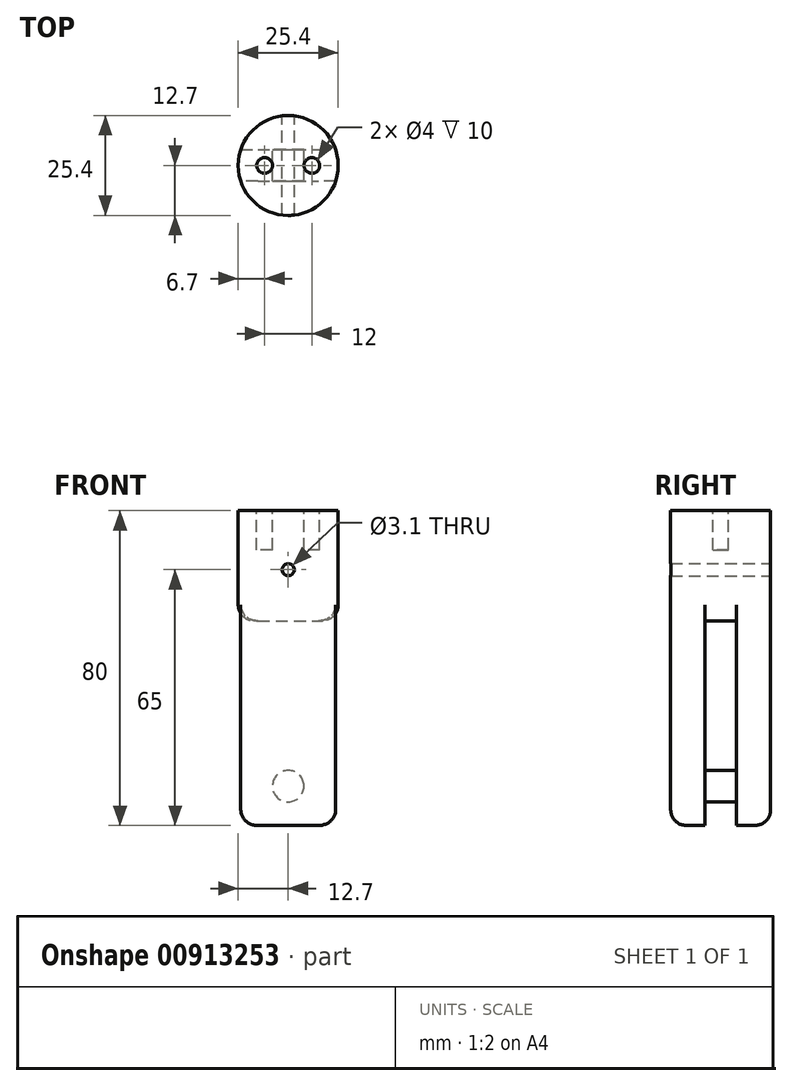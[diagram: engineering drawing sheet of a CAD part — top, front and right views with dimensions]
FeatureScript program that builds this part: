
annotation { "Feature Type Name" : "Feature", "Feature Type Description" : "" }
export const myFeature = defineFeature(function(context is Context, id is Id, definition is map)
    precondition{}
    {
        {
            var Q0;
            Q0=qCreatedBy(makeId("Front.planeOp"),FACE);
            var sketch = newSketch(context, id + "F0", { "sketchPlane" : qUnion([Q0])});
            skCircle(sketch, "E0", {"center": v(0, 0) * mm, "radius": 4 * mm, "construction": true});
            skLineSegment(sketch, "E1.bottom", {"start": v(0, 70) * mm, "end": v(-12.7, 70) * mm});
            skLineSegment(sketch, "E1.top", {"start": v(0, -10) * mm, "end": v(-12.7, -10) * mm});
            skLineSegment(sketch, "E1.left", {"start": v(0, 70) * mm, "end": v(0, -10) * mm});
            skLineSegment(sketch, "E1.right", {"start": v(-12.7, 70) * mm, "end": v(-12.7, -10) * mm});
            skSolve(sketch);
        }
        {
            var Q0;
            Q0=makeQuery(id+"F0.imprint","IMPRINT",FACE,{"disambiguationData":[TD([[makeQuery(id+"F0.imprint","IMPRINT",EDGE,{"derivedFrom":sQuery(id+"F0.wireOp",EDGE,"E1.bottom")}),1.0]])]});
            var Q1;
            Q1=sQuery(id+"F0.wireOp",EDGE,"E1.left");
            revolve(context, id + "F1", {"surfaceOperationType" : NewSurfaceOperationType.NEW, "entities" : qUnion([Q0]), "axis" : qUnion([Q1]), "revolveType" : RevolveType.FULL});
        }
        {
            var Q0;
            Q0=qCreatedBy(makeId("Right.planeOp"),FACE);
            var sketch = newSketch(context, id + "F2", { "sketchPlane" : qUnion([Q0])});
            skPoint(sketch, "E2.0", {"position": v(0, -10) * mm});
            skLineSegment(sketch, "E3.bottom", {"start": v(-4, 42) * mm, "end": v(4, 42) * mm});
            skLineSegment(sketch, "E3.top", {"start": v(-4, -10) * mm, "end": v(4, -10) * mm});
            skLineSegment(sketch, "E3.left", {"start": v(-4, 42) * mm, "end": v(-4, -10) * mm});
            skLineSegment(sketch, "E3.right", {"start": v(4, 42) * mm, "end": v(4, -10) * mm});
            skSolve(sketch);
        }
        {
            var Q0;
            Q0=qSketchRegion(id+"F2",true);
            extrude(context, id + "F3", {"entities" : qUnion([Q0]), "operationType" : NewBodyOperationType.REMOVE, "endBound" : BoundingType.THROUGH_ALL, "oppositeDirection" : true, "depth" : 25 * mm, "offsetDistance" : 25 * mm, "hasSecondDirection" : true, "secondDirectionBound" : SecondDirectionBoundingType.THROUGH_ALL, "secondDirectionOppositeDirection" : false, "secondDirectionDepth" : 25 * mm});
        }
        {
            var Q0;
            Q0=qCreatedBy(makeId("Front.planeOp"),FACE);
            var sketch = newSketch(context, id + "F4", { "sketchPlane" : qUnion([Q0])});
            skCircle(sketch, "E4.0", {"center": v(0, 0) * mm, "radius": 4 * mm});
            skSolve(sketch);
        }
        {
            var Q0;
            Q0=qSketchRegion(id+"F4",true);
            extrude(context, id + "F5", {"entities" : qUnion([Q0]), "operationType" : NewBodyOperationType.ADD, "endBound" : BoundingType.SYMMETRIC, "depth" : 10 * mm, "offsetDistance" : 25 * mm});
        }
        {
            var Q0;
            Q0=makeQuery(id+"F1.opRevolve","SWEPT_FACE",FACE,{"disambiguationData":[OSD([sQuery(id+"F0.wireOp",EDGE,"E1.bottom")])]});
            var sketch = newSketch(context, id + "F6", { "sketchPlane" : qUnion([Q0])});
            skCircle(sketch, "E5", {"center": v(-6, 0) * mm, "radius": 2 * mm});
            skLineSegment(sketch, "E6", {"start": v(0, 0) * mm, "end": v(0, 3.84) * mm});
            skCircle(sketch, "E7.MirrorC", {"center": v(6, 0) * mm, "radius": 2 * mm});
            skSolve(sketch);
        }
        {
            var Q0;
            Q0=qSketchRegion(id+"F6",true);
            extrude(context, id + "F7", {"entities" : qUnion([Q0]), "operationType" : NewBodyOperationType.REMOVE, "oppositeDirection" : true, "depth" : 10 * mm, "offsetDistance" : 25 * mm});
        }
        {
            var Q0;
            Q0=makeQuery(id+"F3.boolean.opBoolean","INTERSECT",EDGE,{"disambiguationData":[OD(0.0)],"derivedFrom":[makeQuery(id+"F1.opRevolve","SWEPT_FACE",FACE,{"disambiguationData":[OSD([sQuery(id+"F0.wireOp",EDGE,"E1.right")])]}),makeQuery(id+"F3.opExtrude","SWEPT_FACE",FACE,{"disambiguationData":[OSD([sQuery(id+"F2.wireOp",EDGE,"E3.bottom")])]})]});
            var Q1;
            Q1=makeQuery(id+"F3.boolean.opBoolean","INTERSECT",EDGE,{"disambiguationData":[OD(1.0)],"derivedFrom":[makeQuery(id+"F1.opRevolve","SWEPT_FACE",FACE,{"disambiguationData":[OSD([sQuery(id+"F0.wireOp",EDGE,"E1.right")])]}),makeQuery(id+"F3.opExtrude","SWEPT_FACE",FACE,{"disambiguationData":[OSD([sQuery(id+"F2.wireOp",EDGE,"E3.bottom")])]})]});
            var Q2;
            {var subQ0=sQuery(id+"F0.wireOp",EDGE,"E1.top");var subQ1=sQuery(id+"F0.wireOp",EDGE,"E1.right");Q2=makeQuery(id+"F3.boolean.opBoolean","SPLIT",EDGE,{"disambiguationData":[TD([makeQuery(id+"F3.opExtrude","SWEPT_FACE",FACE,{"disambiguationData":[OSD([sQuery(id+"F2.wireOp",EDGE,"E3.left")])]})])],"derivedFrom":makeQuery(id+"F1.opRevolve","SWEPT_EDGE",EDGE,{"disambiguationData":[OSD([subQ0,subQ1])]})});}
            var Q3;
            {var subQ0=sQuery(id+"F0.wireOp",EDGE,"E1.top");var subQ1=sQuery(id+"F0.wireOp",EDGE,"E1.right");Q3=makeQuery(id+"F3.boolean.opBoolean","SPLIT",EDGE,{"disambiguationData":[TD([makeQuery(id+"F3.opExtrude","SWEPT_FACE",FACE,{"disambiguationData":[OSD([sQuery(id+"F2.wireOp",EDGE,"E3.right")])]})])],"derivedFrom":makeQuery(id+"F1.opRevolve","SWEPT_EDGE",EDGE,{"disambiguationData":[OSD([subQ0,subQ1])]})});}
            fillet(context, id + "F8", {"entities" : qUnion([Q0, Q1, Q2, Q3]), "radius" : 4 * mm, "tangentPropagation" : true, "allowEdgeOverflow" : false});
        }
        {
            var Q0;
            Q0=qCreatedBy(makeId("Front.planeOp"),FACE);
            var sketch = newSketch(context, id + "F9", { "sketchPlane" : qUnion([Q0])});
            skLineSegment(sketch, "E8.0", {"start": v(-12.7, 70) * mm, "end": v(12.7, 70) * mm, "construction": true});
            skLineSegment(sketch, "E9", {"start": v(0, 70) * mm, "end": v(0, 55) * mm, "construction": true});
            skCircle(sketch, "E10", {"center": v(0, 55) * mm, "radius": 1.55 * mm});
            skSolve(sketch);
        }
        {
            var Q0;
            Q0=qSketchRegion(id+"F9",true);
            extrude(context, id + "F10", {"entities" : qUnion([Q0]), "operationType" : NewBodyOperationType.REMOVE, "endBound" : BoundingType.THROUGH_ALL, "depth" : 30 * mm, "offsetDistance" : 25 * mm, "hasSecondDirection" : true, "secondDirectionBound" : SecondDirectionBoundingType.THROUGH_ALL, "secondDirectionOppositeDirection" : true, "secondDirectionDepth" : 25 * mm});
        }
    });
